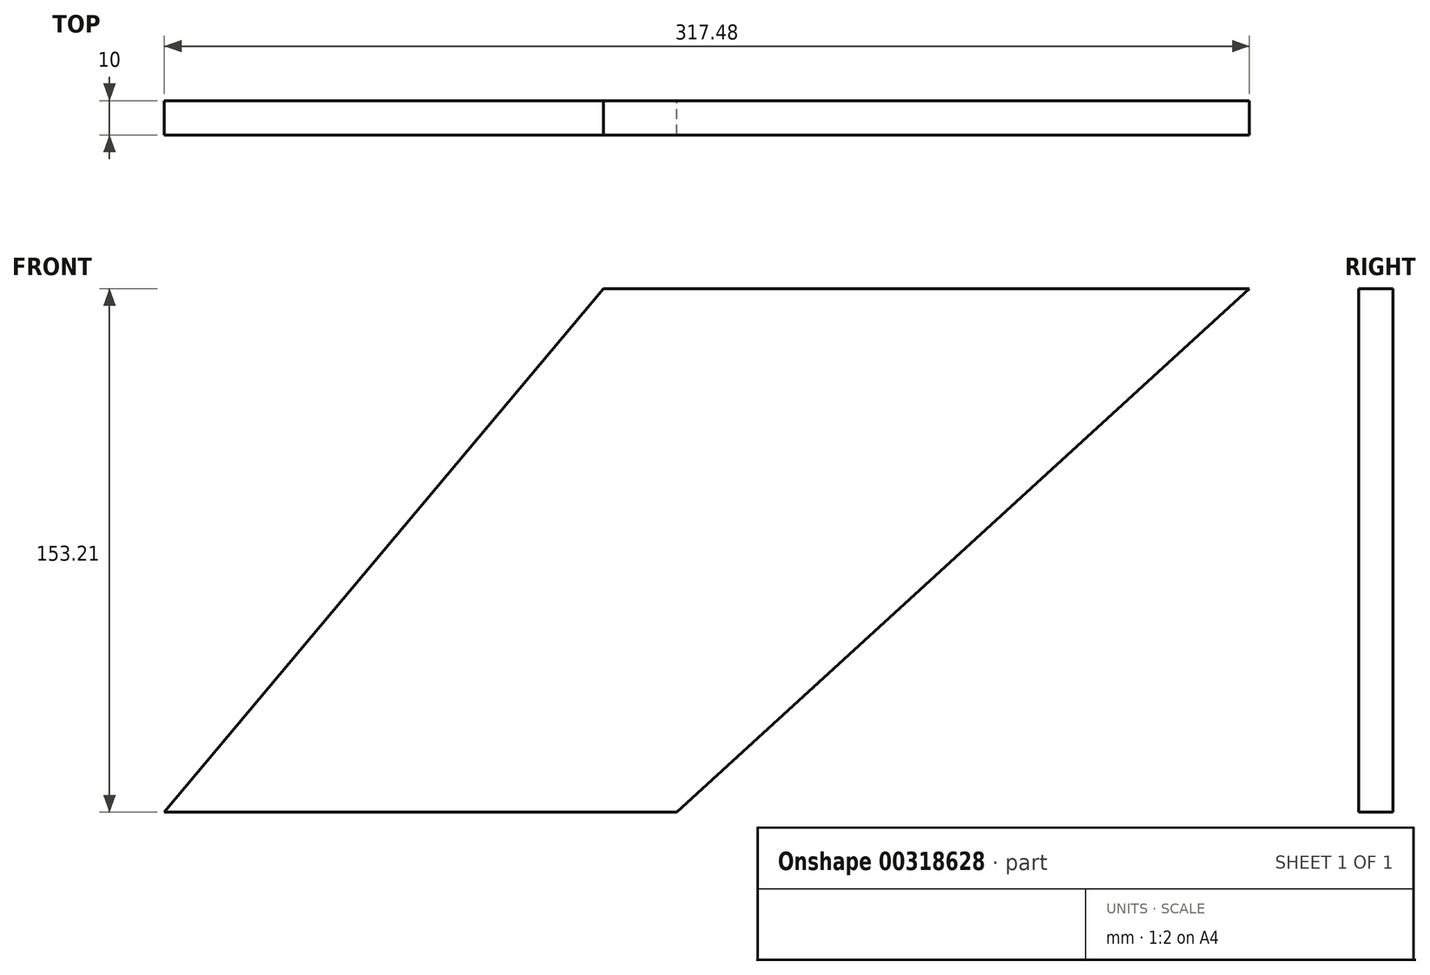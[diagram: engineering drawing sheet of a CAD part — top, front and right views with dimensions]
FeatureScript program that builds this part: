
annotation { "Feature Type Name" : "Feature", "Feature Type Description" : "" }
export const myFeature = defineFeature(function(context is Context, id is Id, definition is map)
    precondition{}
    {
        {
            var Q0;
            Q0=qCreatedBy(makeId("Front.planeOp"),FACE);
            var sketch = newSketch(context, id + "F0", { "sketchPlane" : qUnion([Q0])});
            skLineSegment(sketch, "E0", {"start": v(0, 0) * mm, "end": v(150, 0) * mm});
            skLineSegment(sketch, "E1", {"start": v(150, 0) * mm, "end": v(317.48, 153.2) * mm});
            skLineSegment(sketch, "E2", {"start": v(317.48, 153.2) * mm, "end": v(128.56, 153.2) * mm});
            skLineSegment(sketch, "E3", {"start": v(128.56, 153.2) * mm, "end": v(0, 0) * mm});
            skSolve(sketch);
        }
        {
            var Q0;
            Q0 = qSketchRegion(id + "F0", true);
            var Q1;
            Q1=makeQuery(id+"F0.imprint","IMPRINT",FACE,{"disambiguationData":[TD([[makeQuery(id+"F0.imprint","IMPRINT",EDGE,{"derivedFrom":sQuery(id+"F0.wireOp",EDGE,"E0")}),1.0]])]});
            extrude(context, id + "F1", {"entities" : qUnion([Q0, Q1]), "depth" : 10 * mm});
        }
    });
